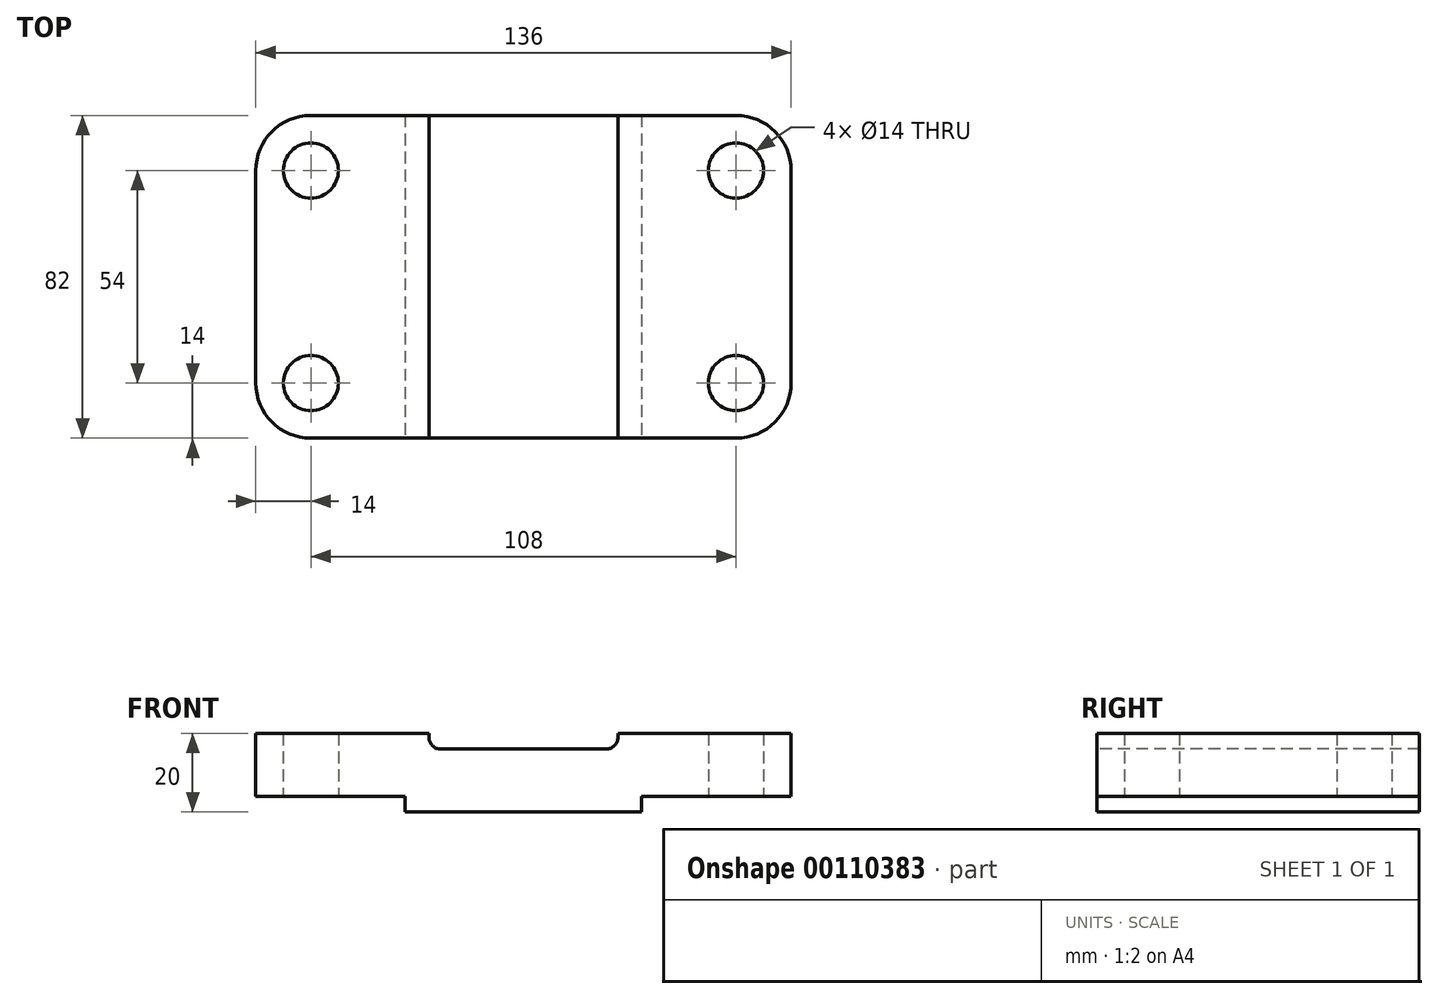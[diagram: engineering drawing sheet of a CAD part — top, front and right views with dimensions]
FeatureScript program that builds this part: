
annotation { "Feature Type Name" : "Feature", "Feature Type Description" : "" }
export const myFeature = defineFeature(function(context is Context, id is Id, definition is map)
    precondition{}
    {
        {
            var Q0;
            Q0=qCreatedBy(makeId("Front.planeOp"),FACE);
            var sketch = newSketch(context, id + "F0", { "sketchPlane" : qUnion([Q0])});
            skLineSegment(sketch, "E0", {"start": v(0, 0) * mm, "end": v(0, 16) * mm});
            skLineSegment(sketch, "E1", {"start": v(0, 16) * mm, "end": v(44, 16) * mm});
            skLineSegment(sketch, "E2", {"start": v(44, 16) * mm, "end": v(44, 12) * mm});
            skLineSegment(sketch, "E3", {"start": v(44, 12) * mm, "end": v(92, 12) * mm});
            skLineSegment(sketch, "E4", {"start": v(92, 12) * mm, "end": v(92, 16) * mm});
            skLineSegment(sketch, "E5", {"start": v(92, 16) * mm, "end": v(136, 16) * mm});
            skLineSegment(sketch, "E6", {"start": v(136, 16) * mm, "end": v(136, 0) * mm});
            skLineSegment(sketch, "E7", {"start": v(136, 0) * mm, "end": v(98, 0) * mm});
            skLineSegment(sketch, "E8", {"start": v(98, 0) * mm, "end": v(98, -4) * mm});
            skLineSegment(sketch, "E9", {"start": v(98, -4) * mm, "end": v(38, -4) * mm});
            skLineSegment(sketch, "E10", {"start": v(38, -4) * mm, "end": v(38, 0) * mm});
            skLineSegment(sketch, "E11", {"start": v(38, 0) * mm, "end": v(0, 0) * mm});
            skSolve(sketch);
        }
        {
            var Q0;
            Q0 = qSketchRegion(id + "F0", true);
            extrude(context, id + "F1", {"entities" : qUnion([Q0]), "oppositeDirection" : true, "depth" : 82 * mm});
        }
        {
            var Q0;
            Q0=makeQuery(id+"F1.opExtrude","SWEPT_EDGE",EDGE,{"disambiguationData":[OSD([sQuery(id+"F0.wireOp",EDGE,"E2"),sQuery(id+"F0.wireOp",EDGE,"E3")])]});
            var Q1;
            Q1=makeQuery(id+"F1.opExtrude","SWEPT_EDGE",EDGE,{"disambiguationData":[OSD([sQuery(id+"F0.wireOp",EDGE,"E3"),sQuery(id+"F0.wireOp",EDGE,"E4")])]});
            fillet(context, id + "F2", {"entities" : qUnion([Q0, Q1]), "radius" : 3 * mm, "tangentPropagation" : true, "allowEdgeOverflow" : false});
        }
        {
            var Q0;
            Q0=qCreatedBy(makeId("Top.planeOp"),FACE);
            var sketch = newSketch(context, id + "F3", { "sketchPlane" : qUnion([Q0])});
            skCircle(sketch, "E12", {"center": v(14, 14) * mm, "radius": 7 * mm});
            skCircle(sketch, "E13.1.0.0", {"center": v(122, 14) * mm, "radius": 7 * mm});
            skLineSegment(sketch, "E13.direction1", {"start": v(14, 14) * mm, "end": v(122, 14) * mm, "construction": true});
            skCircle(sketch, "E14.0.1.0", {"center": v(14, 68) * mm, "radius": 7 * mm});
            skCircle(sketch, "E14.0.1.1", {"center": v(122, 68) * mm, "radius": 7 * mm});
            skLineSegment(sketch, "E14.direction2", {"start": v(14, 14) * mm, "end": v(14, 68) * mm, "construction": true});
            skLineSegment(sketch, "E15", {"start": v(14, 68) * mm, "end": v(122, 68) * mm, "construction": true});
            skSolve(sketch);
        }
        {
            var Q0;
            Q0 = qSketchRegion(id + "F3", true);
            extrude(context, id + "F4", {"entities" : qUnion([Q0]), "operationType" : NewBodyOperationType.REMOVE, "endBound" : BoundingType.THROUGH_ALL, "depth" : 25 * mm});
        }
        {
            var Q0;
            Q0=makeQuery(id+"F1.opExtrude","CAP_EDGE",EDGE,{"disambiguationData":[OSD([sQuery(id+"F0.wireOp",EDGE,"E0")])],"isStart":true});
            var Q1;
            Q1=makeQuery(id+"F1.opExtrude","CAP_EDGE",EDGE,{"disambiguationData":[OSD([sQuery(id+"F0.wireOp",EDGE,"E0")])],"isStart":false});
            var Q2;
            Q2=makeQuery(id+"F1.opExtrude","CAP_EDGE",EDGE,{"disambiguationData":[OSD([sQuery(id+"F0.wireOp",EDGE,"E6")])],"isStart":true});
            var Q3;
            Q3=makeQuery(id+"F1.opExtrude","CAP_EDGE",EDGE,{"disambiguationData":[OSD([sQuery(id+"F0.wireOp",EDGE,"E6")])],"isStart":false});
            fillet(context, id + "F5", {"entities" : qUnion([Q0, Q1, Q2, Q3]), "radius" : 14 * mm, "tangentPropagation" : true, "allowEdgeOverflow" : false});
        }
    });
